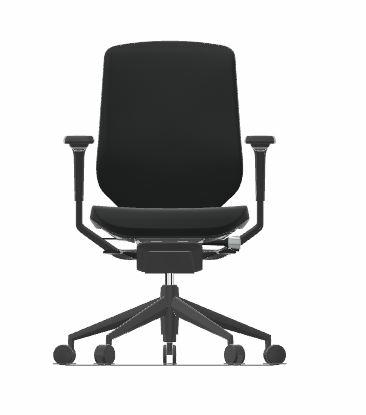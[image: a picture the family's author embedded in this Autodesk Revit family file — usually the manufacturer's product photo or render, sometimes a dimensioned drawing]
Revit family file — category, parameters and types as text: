
# Revit family: 08 Chair
name_source: partatom
category: Furniture
units: mm (PartAtom-declared; Revit-internal decimal feet)

## family parameters
Always vertical = Yes
Cut with Voids When Loaded = No
OmniClass Number = 23.40.20.00
OmniClass Title = General Furniture and Specialties
Room Calculation Point = No
Shared = No
Work Plane-Based = No

## types (1)
- Armrest - Tex back
    Armrest = Yes
    Armrest Material = Black Polypropylene
    Assembly Code = E2020200
    Back Material = String:31(EN)
    Base Height = 36 cm
    Catálogo Producto = https://actiucdn.net
    Certificados = https://actiucdn.net
    Chair Base Material = Black Aluminum
    Chair Frame Material = Black
    Chair Parts Material = Black Polypropylene
    Default Elevation = 0 cm
    Description = The strong nylon fabric used in the back is always adjusted to the user's movement, providing back perspiration and keeping a constant temperature.
    Headrest Material = String:31(EN)
    Manufacturer = ACTIU
    Model = TNK
    No Armrest = No
    Seat Height = 53 cm
    Seat Material = String:31(EN)
    TEX Back = Yes
    Total Height = 123 cm
    URL = https://www.actiu.com
    URL Producto = https://www.actiu.com
    Upholstered back = No
